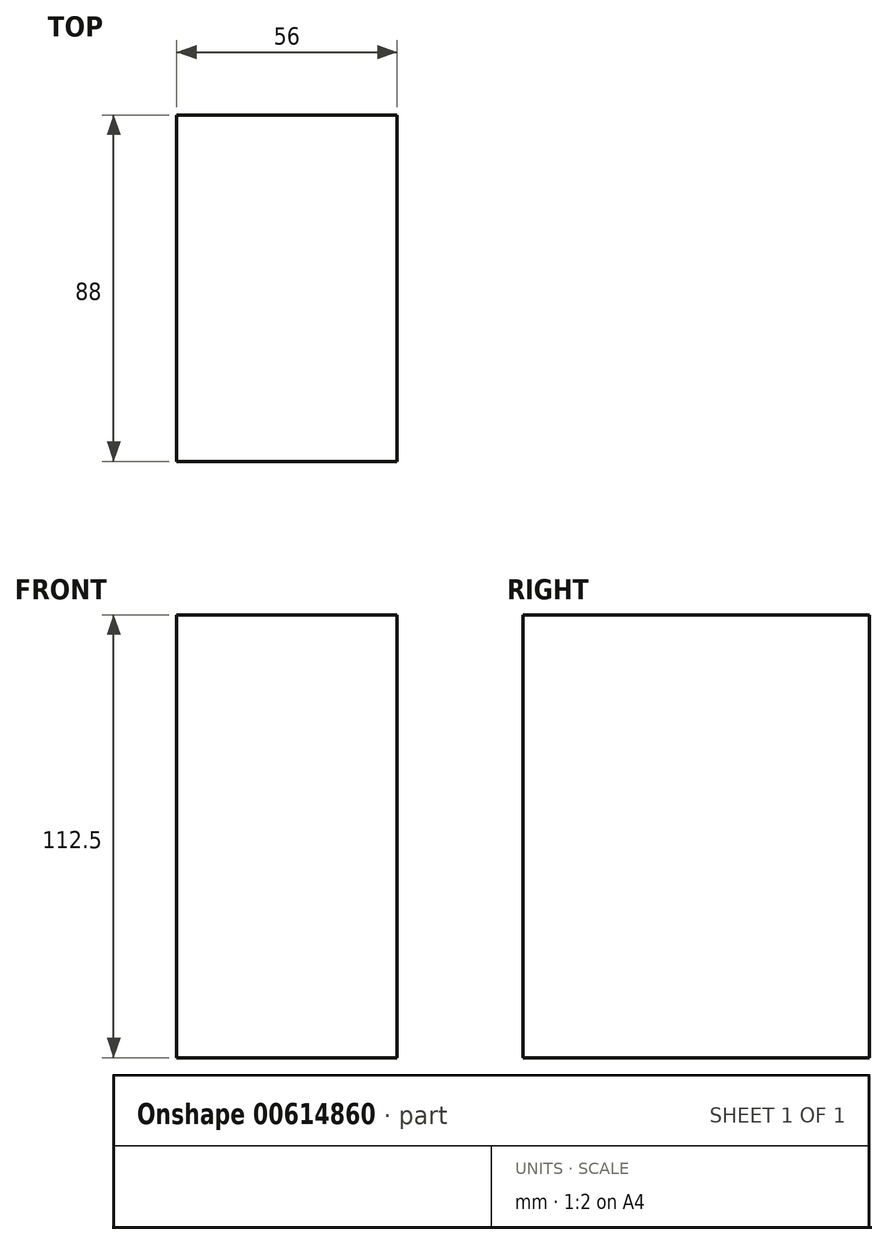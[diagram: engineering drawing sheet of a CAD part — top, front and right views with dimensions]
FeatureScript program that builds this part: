
annotation { "Feature Type Name" : "Feature", "Feature Type Description" : "" }
export const myFeature = defineFeature(function(context is Context, id is Id, definition is map)
    precondition{}
    {
        {
            var Q0;
            Q0=qCreatedBy(makeId("Front.planeOp"),FACE);
            var sketch = newSketch(context, id + "F0", { "sketchPlane" : qUnion([Q0])});
            skLineSegment(sketch, "E0.bottom", {"start": v(-29.9, 60.65) * mm, "end": v(26.1, 60.65) * mm});
            skLineSegment(sketch, "E0.top", {"start": v(-29.9, -51.85) * mm, "end": v(26.1, -51.85) * mm});
            skLineSegment(sketch, "E0.left", {"start": v(-29.9, 60.65) * mm, "end": v(-29.9, -51.85) * mm});
            skLineSegment(sketch, "E0.right", {"start": v(26.1, 60.65) * mm, "end": v(26.1, -51.85) * mm});
            skSolve(sketch);
        }
        {
            var Q0;
            Q0=sQuery(id+"F0.wireOp",EDGE,"E0.right");
            var Q1;
            Q1=sQuery(id+"F0.wireOp",EDGE,"E0.bottom");
            var Q2;
            Q2=sQuery(id+"F0.wireOp",EDGE,"E0.left");
            var Q3;
            Q3=sQuery(id+"F0.wireOp",EDGE,"E0.top");
            extrude(context, id + "F1", {"bodyType" : ToolBodyType.SURFACE, "surfaceEntities" : qUnion([Q0, Q1, Q2, Q3]), "oppositeDirection" : true, "depth" : 88 * mm, "offsetDistance" : 25 * mm});
        }
    });
